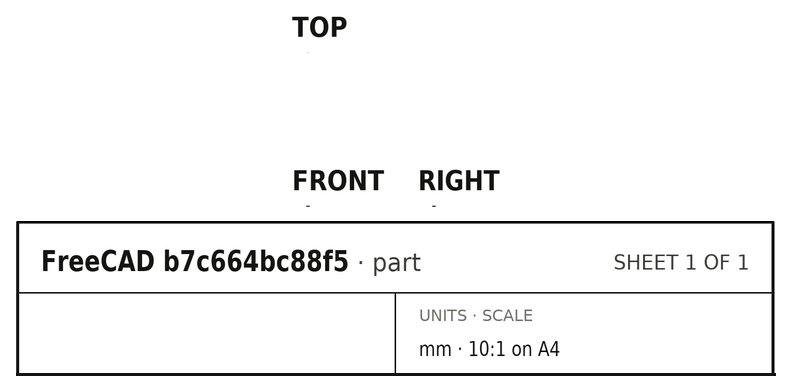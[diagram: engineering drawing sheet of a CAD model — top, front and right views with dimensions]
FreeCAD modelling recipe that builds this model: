
FCSTD DOCUMENT  (FreeCAD 0.21R33694 (Git))
Label: step2
License: All rights reserved
LicenseURL: http://en.wikipedia.org/wiki/All_rights_reserved
objects: Part::Part2DObjectPython×7, Part::Extrusion×4, App::FeaturePython×4, Part::FeaturePython×2, Part::Cut×1
note: 14 computed .brp shape members not serialized (recipe doc carries the construction recipe); baked Part::Feature solids carry a one-line shape summary decoded from their .brp

FEATURE [Part::Part2DObjectPython] Rectangle  # Draft 2D object (typed FeaturePython)
  Area = 3.556
  ChamferSize = 0
  Columns = 1
  FilletRadius = 0
  Height = 1.778
  Length = 2
  MakeFace = true
  Rows = 1
FEATURE [Part::Part2DObjectPython] Rectangle001  # Draft 2D object (typed FeaturePython)
  Area = 3.556
  ChamferSize = 0
  Columns = 1
  FilletRadius = 0
  Height = 1.778
  Length = 2
  MakeFace = true
  Rows = 1
FEATURE [Part::Extrusion] Extrude
  Base = -> Rectangle
  Dir = (0,0,1)
  DirMode = 2
  FaceMakerClass = Part::FaceMakerBullseye
  LengthFwd = 0.254
  LengthRev = 0
  Solid = false
  Symmetric = false
FEATURE [Part::Extrusion] Extrude001
  Base = -> Rectangle001
  Dir = (0,0,1)
  DirMode = 2
  FaceMakerClass = Part::FaceMakerBullseye
  LengthFwd = 3.429
  LengthRev = 0
  Placement = pos=(0,0,0.254) rot=(0,0,1;0rad)
  Solid = false
  Symmetric = false
FEATURE [Part::Extrusion] Extrude002
  Base = -> Rectangle001
  Dir = (0,0,1)
  DirMode = 2
  FaceMakerClass = Part::FaceMakerBullseye
  LengthFwd = -3.429
  LengthRev = 0
  Solid = false
  Symmetric = false
FEATURE [Part::Part2DObjectPython] Wire001  # Draft 2D object (typed FeaturePython)
  Area = 3.06705
  ChamferSize = 0
  Closed = true
  End = (1.875,0.889,0.254)
  FilletRadius = 0
  Length = 7.306
  MakeFace = true
  Placement = pos=(1.875,0,0.254) rot=(0,0,1;0rad)
  Points = (6) [(0,0,0),(-1.875,0,0),(-1.875,1.778,0),(-0.3,1.778,0),(-0.3,0.889,0),(0,0.889,0)]
  Start = (1.875,0,0.254)
  Subdivisions = 0
FEATURE [Part::Part2DObjectPython] Rectangle002  label="_P1"  # Draft 2D object (typed FeaturePython)
  Area = 1.4224e-05
  ChamferSize = 0
  Columns = 1
  FilletRadius = 0
  Height = 0.007112
  Length = 0.002
  MakeFace = true
  Placement = pos=(0,0,-0.003429) rot=(1,0,0;1.5708rad)
  Rows = 1
FEATURE [Part::Part2DObjectPython] Line  label="_PV1"  # Draft 2D object (typed FeaturePython)
  Area = 0
  ChamferSize = 0
  Closed = false
  End = (0.002,0,0.000254)
  FilletRadius = 0
  Length = 0.000125
  MakeFace = true
  Placement = pos=(0.001875,0,0.000254) rot=(0,0,1;0rad)
  Points = (2) [(0,0,0),(0.000125,0,2.36356e-17)]
  Start = (0.001875,0,0.000254)
  Subdivisions = 0
FEATURE [Part::Part2DObjectPython] Rectangle004  label="_P2"  # Draft 2D object (typed FeaturePython)
  Area = 1.4224e-05
  ChamferSize = 0
  Columns = 1
  FilletRadius = 0
  Height = 0.007112
  Length = 0.002
  MakeFace = true
  Placement = pos=(0.002,0.001778,-0.003429) rot=(0,0.707107,0.707107;3.14159rad)
  Rows = 1
FEATURE [Part::Part2DObjectPython] Line001  label="_PV2"  # Draft 2D object (typed FeaturePython)
  Area = 0
  ChamferSize = 0
  Closed = false
  End = (0.002,0.001778,0.000254)
  FilletRadius = 0
  Length = 0.000425
  MakeFace = true
  Placement = pos=(0.001575,0.001778,0.000254) rot=(0,0.707107,0.707107;3.14159rad)
  Points = (2) [(0,0,0),(-0.000425,2.36356e-17,0)]
  Start = (0.001575,0.001778,0.000254)
  Subdivisions = 0
FEATURE [App::FeaturePython] Text  label="_S1(PV){1}"  # WARN: FeaturePython — macro-defined, semantics opaque (R4)
  Placement = pos=(0.00384868,0.001778,-0.00189626) rot=(0,0.707107,0.707107;3.14159rad)
  Text = .
FEATURE [App::FeaturePython] Text001  label="_S2(PV){2}"  # WARN: FeaturePython — macro-defined, semantics opaque (R4)
  Placement = pos=(0.00384868,0.001778,-0.00189626) rot=(0,0.707107,0.707107;3.14159rad)
  Text = .
FEATURE [App::FeaturePython] Text002  label="_M1(1,voltage){V1}"  # WARN: FeaturePython — macro-defined, semantics opaque (R4)
  Placement = pos=(0.00384868,0.001778,-0.00189626) rot=(0,0.707107,0.707107;3.14159rad)
  Text = .
FEATURE [App::FeaturePython] Text003  label="_M2(2,voltage){V2}"  # WARN: FeaturePython — macro-defined, semantics opaque (R4)
  Placement = pos=(0.00384868,0.001778,-0.00189626) rot=(0,0.707107,0.707107;3.14159rad)
  Text = .
FEATURE [Part::Extrusion] Extrude003
  Base = -> Wire001
  Dir = (0,0,1)
  DirMode = 2
  FaceMakerClass = Part::FaceMakerBullseye
  LengthFwd = 0.0125
  LengthRev = 0
  Solid = false
  Symmetric = false
FEATURE [Part::Cut] Cut
  Base = -> Extrude001
  Tool = -> Extrude003
FEATURE [Part::FeaturePython] BooleanFragments  # WARN: FeaturePython — macro-defined, semantics opaque (R4)
  Mode = 0
  Objects = -> [Extrude,Extrude002,Cut]
  Tolerance = 0
FEATURE [Part::FeaturePython] Clone  label="scaled"  # Draft clone (typed FeaturePython)
  AttacherType = Attacher::AttachEngine3D
  Fuse = false
  Objects = -> [BooleanFragments]
  Scale = (0.001,0.001,0.001)
